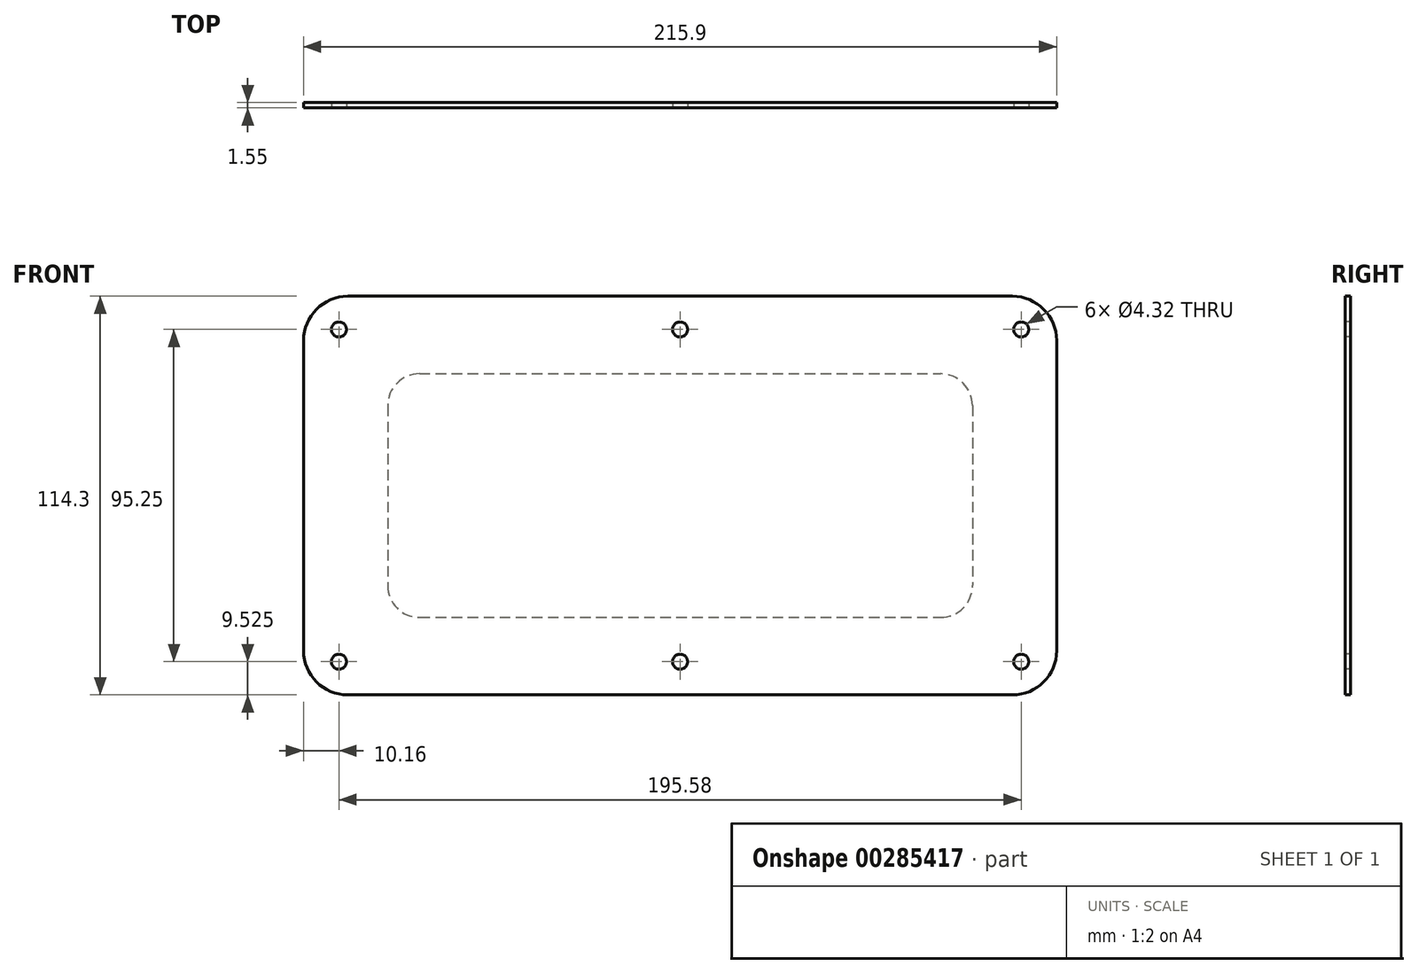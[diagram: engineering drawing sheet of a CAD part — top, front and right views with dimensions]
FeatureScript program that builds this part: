
annotation { "Feature Type Name" : "Feature", "Feature Type Description" : "" }
export const myFeature = defineFeature(function(context is Context, id is Id, definition is map)
    precondition{}
    {
        {
            var Q0;
            Q0=qCreatedBy(makeId("Front.planeOp"),FACE);
            var sketch = newSketch(context, id + "F0", { "sketchPlane" : qUnion([Q0])});
            skLineSegment(sketch, "E0.bottom", {"start": v(33.27, -22.23) * mm, "end": v(182.63, -22.23) * mm, "construction": true});
            skLineSegment(sketch, "E0.top", {"start": v(33.27, -92.08) * mm, "end": v(182.63, -92.08) * mm, "construction": true});
            skLineSegment(sketch, "E0.left", {"start": v(24.13, -31.37) * mm, "end": v(24.13, -82.93) * mm, "construction": true});
            skLineSegment(sketch, "E0.right", {"start": v(191.77, -31.37) * mm, "end": v(191.77, -82.93) * mm, "construction": true});
            skPoint(sketch, "E1.visualSharp", {"position": v(24.13, -22.23) * mm});
            skArc(sketch, "E1.filletArc", {"start": v(33.27, -22.23) * mm, "mid": v(26.8, -24.9) * mm, "end": v(24.13, -31.37) * mm, "construction": true});
            skPoint(sketch, "E2.visualSharp", {"position": v(191.77, -22.23) * mm});
            skArc(sketch, "E2.filletArc", {"start": v(191.77, -31.37) * mm, "mid": v(189.1, -24.9) * mm, "end": v(182.63, -22.22) * mm, "construction": true});
            skPoint(sketch, "E3.visualSharp", {"position": v(191.77, -92.08) * mm});
            skArc(sketch, "E3.filletArc", {"start": v(182.63, -92.08) * mm, "mid": v(189.1, -89.4) * mm, "end": v(191.77, -82.93) * mm, "construction": true});
            skPoint(sketch, "E4.visualSharp", {"position": v(24.13, -92.08) * mm});
            skArc(sketch, "E4.filletArc", {"start": v(24.13, -82.93) * mm, "mid": v(26.8, -89.4) * mm, "end": v(33.27, -92.07) * mm, "construction": true});
            skLineSegment(sketch, "E5.bottom", {"start": v(12.7, 0) * mm, "end": v(203.2, 0) * mm});
            skLineSegment(sketch, "E5.top", {"start": v(12.7, -114.3) * mm, "end": v(203.2, -114.3) * mm});
            skLineSegment(sketch, "E5.left", {"start": v(0, -12.7) * mm, "end": v(0, -101.6) * mm});
            skLineSegment(sketch, "E5.right", {"start": v(215.9, -12.7) * mm, "end": v(215.9, -101.6) * mm});
            skPoint(sketch, "E6.visualSharp", {"position": v(0, 0) * mm});
            skArc(sketch, "E6.filletArc", {"start": v(12.7, 0) * mm, "mid": v(3.72, -3.72) * mm, "end": v(0, -12.7) * mm});
            skPoint(sketch, "E7.visualSharp", {"position": v(215.9, 0) * mm});
            skArc(sketch, "E7.filletArc", {"start": v(215.9, -12.7) * mm, "mid": v(212.18, -3.72) * mm, "end": v(203.2, 0) * mm});
            skPoint(sketch, "E8.visualSharp", {"position": v(215.9, -114.3) * mm});
            skArc(sketch, "E8.filletArc", {"start": v(203.2, -114.3) * mm, "mid": v(212.18, -110.58) * mm, "end": v(215.9, -101.6) * mm});
            skPoint(sketch, "E9.visualSharp", {"position": v(0, -114.3) * mm});
            skArc(sketch, "E9.filletArc", {"start": v(0, -101.6) * mm, "mid": v(3.72, -110.58) * mm, "end": v(12.7, -114.3) * mm});
            skLineSegment(sketch, "E10", {"start": v(107.95, 0) * mm, "end": v(107.95, -114.3) * mm, "construction": true});
            skLineSegment(sketch, "E11", {"start": v(0, -57.15) * mm, "end": v(215.9, -57.15) * mm, "construction": true});
            skPoint(sketch, "E12", {"position": v(107.95, -22.23) * mm});
            skPoint(sketch, "E13", {"position": v(191.77, -57.15) * mm});
            skPoint(sketch, "E14", {"position": v(10.16, -9.52) * mm});
            skPoint(sketch, "E15", {"position": v(107.95, -9.52) * mm});
            skPoint(sketch, "E16", {"position": v(205.74, -9.52) * mm});
            skPoint(sketch, "E17", {"position": v(205.74, -104.78) * mm});
            skPoint(sketch, "E18", {"position": v(107.95, -104.78) * mm});
            skPoint(sketch, "E19", {"position": v(10.16, -104.78) * mm});
            skLineSegment(sketch, "E20", {"start": v(10.16, -9.52) * mm, "end": v(10.16, -104.78) * mm, "construction": true});
            skSolve(sketch);
        }
        {
            var Q0;
            Q0=makeQuery(id+"F0.imprint","IMPRINT",FACE,{"disambiguationData":[TD([[makeQuery(id+"F0.imprint","IMPRINT",EDGE,{"derivedFrom":sQuery(id+"F0.wireOp",EDGE,"E5.bottom")}),-1.0]])]});
            extrude(context, id + "F1", {"entities" : qUnion([Q0]), "depth" : 1.52 * mm});
        }
        {
            var Q0;
            Q0=makeQuery(id+"F1.opExtrude","CAP_FACE",FACE,{"disambiguationData":[OSD([sQuery(id+"F0.wireOp",EDGE,"E5.bottom"),sQuery(id+"F0.wireOp",EDGE,"E5.top"),sQuery(id+"F0.wireOp",EDGE,"E5.left"),sQuery(id+"F0.wireOp",EDGE,"E5.right"),sQuery(id+"F0.wireOp",EDGE,"E6.filletArc"),sQuery(id+"F0.wireOp",EDGE,"E7.filletArc"),sQuery(id+"F0.wireOp",EDGE,"E8.filletArc"),sQuery(id+"F0.wireOp",EDGE,"E9.filletArc")])],"isStart":false});
            var sketch = newSketch(context, id + "F2", { "sketchPlane" : qUnion([Q0])});
            skPoint(sketch, "E21", {"position": v(10.16, -9.52) * mm});
            skPoint(sketch, "E22", {"position": v(107.95, -9.52) * mm});
            skPoint(sketch, "E23", {"position": v(205.74, -9.52) * mm});
            skPoint(sketch, "E24", {"position": v(205.74, -104.78) * mm});
            skPoint(sketch, "E25", {"position": v(107.95, -104.78) * mm});
            skPoint(sketch, "E26", {"position": v(10.16, -104.78) * mm});
            skSolve(sketch);
        }
        {
            var Q0;
            Q0=sQuery(id+"F2.wireOp",VERTEX,"E21");
            var Q1;
            Q1=sQuery(id+"F2.wireOp",VERTEX,"E22");
            var Q2;
            Q2=sQuery(id+"F2.wireOp",VERTEX,"E23");
            var Q3;
            Q3=sQuery(id+"F2.wireOp",VERTEX,"E24");
            var Q4;
            Q4=sQuery(id+"F2.wireOp",VERTEX,"E25");
            var Q5;
            Q5=sQuery(id+"F2.wireOp",VERTEX,"E26");
            var Q6;
            Q6=makeQuery(id+"F1.opExtrude","SWEPT_BODY",BODY,{"disambiguationData":[OSD([sQuery(id+"F0.wireOp",EDGE,"E5.bottom"),sQuery(id+"F0.wireOp",EDGE,"E5.top"),sQuery(id+"F0.wireOp",EDGE,"E5.left"),sQuery(id+"F0.wireOp",EDGE,"E5.right"),sQuery(id+"F0.wireOp",EDGE,"E6.filletArc"),sQuery(id+"F0.wireOp",EDGE,"E7.filletArc"),sQuery(id+"F0.wireOp",EDGE,"E8.filletArc"),sQuery(id+"F0.wireOp",EDGE,"E9.filletArc")])]});
            hole(context, id + "F3", {"style" : HoleStyle.SIMPLE, "endStyle" : HoleEndStyle.THROUGH, "standardTappedOrClearance" : lookupTablePath({ "standard" : "ANSI", "fit" : "Close", "size" : "#8", "type" : "Clearance" }), "standardBlindInLast" : lookupTablePath({ "fit" : "Close", "standard" : "ANSI", "size" : "#8", "type" : "Clearance" }), "holeDiameter" : 4.32 * mm, "isTappedThrough" : true, "tappedDepth" : 2.4 * mm, "tapClearance" : 3, "startFromSketch" : true, "locations" : qUnion([Q0, Q1, Q2, Q3, Q4, Q5]), "scope" : qUnion([Q6]), "majorDiameter" : 6.35 * mm});
        }
        {
            var Q0;
            Q0=makeQuery(id+"F1.opExtrude","CAP_FACE",FACE,{"disambiguationData":[OSD([sQuery(id+"F0.wireOp",EDGE,"E5.bottom"),sQuery(id+"F0.wireOp",EDGE,"E5.top"),sQuery(id+"F0.wireOp",EDGE,"E5.left"),sQuery(id+"F0.wireOp",EDGE,"E5.right"),sQuery(id+"F0.wireOp",EDGE,"E6.filletArc"),sQuery(id+"F0.wireOp",EDGE,"E7.filletArc"),sQuery(id+"F0.wireOp",EDGE,"E8.filletArc"),sQuery(id+"F0.wireOp",EDGE,"E9.filletArc")])],"isStart":true});
            var sketch = newSketch(context, id + "F4", { "sketchPlane" : qUnion([Q0])});
            skLineSegment(sketch, "E27.0", {"start": v(-33.27, -22.23) * mm, "end": v(-182.63, -22.23) * mm});
            skArc(sketch, "E27.1", {"start": v(-33.27, -22.23) * mm, "mid": v(-26.8, -24.9) * mm, "end": v(-24.13, -31.37) * mm});
            skLineSegment(sketch, "E27.2", {"start": v(-24.13, -31.37) * mm, "end": v(-24.13, -82.93) * mm});
            skArc(sketch, "E27.3", {"start": v(-24.13, -82.93) * mm, "mid": v(-26.8, -89.4) * mm, "end": v(-33.27, -92.07) * mm});
            skLineSegment(sketch, "E27.4", {"start": v(-33.27, -92.08) * mm, "end": v(-182.63, -92.08) * mm});
            skArc(sketch, "E27.5", {"start": v(-182.63, -92.08) * mm, "mid": v(-189.1, -89.4) * mm, "end": v(-191.77, -82.93) * mm});
            skLineSegment(sketch, "E27.6", {"start": v(-191.77, -31.37) * mm, "end": v(-191.77, -82.93) * mm});
            skArc(sketch, "E27.7", {"start": v(-191.77, -31.37) * mm, "mid": v(-189.1, -24.9) * mm, "end": v(-182.63, -22.22) * mm});
            skLineSegment(sketch, "E28.0", {"start": v(0, -12.7) * mm, "end": v(0, -101.6) * mm});
            skArc(sketch, "E28.1", {"start": v(-12.7, 0) * mm, "mid": v(-3.72, -3.72) * mm, "end": v(0, -12.7) * mm});
            skLineSegment(sketch, "E28.2", {"start": v(-12.7, 0) * mm, "end": v(-203.2, 0) * mm});
            skArc(sketch, "E28.3", {"start": v(-215.9, -12.7) * mm, "mid": v(-212.18, -3.72) * mm, "end": v(-203.2, 0) * mm});
            skLineSegment(sketch, "E28.4", {"start": v(-215.9, -12.7) * mm, "end": v(-215.9, -101.6) * mm});
            skArc(sketch, "E28.5", {"start": v(-203.2, -114.3) * mm, "mid": v(-212.18, -110.58) * mm, "end": v(-215.9, -101.6) * mm});
            skLineSegment(sketch, "E28.6", {"start": v(-12.7, -114.3) * mm, "end": v(-203.2, -114.3) * mm});
            skArc(sketch, "E28.7", {"start": v(0, -101.6) * mm, "mid": v(-3.72, -110.58) * mm, "end": v(-12.7, -114.3) * mm});
            skCircle(sketch, "E29.0", {"center": v(-205.74, -9.52) * mm, "radius": 2.16 * mm});
            skCircle(sketch, "E30.0", {"center": v(-107.95, -9.52) * mm, "radius": 2.16 * mm});
            skCircle(sketch, "E31.0", {"center": v(-10.16, -9.52) * mm, "radius": 2.16 * mm});
            skCircle(sketch, "E32.0", {"center": v(-10.16, -104.78) * mm, "radius": 2.16 * mm});
            skCircle(sketch, "E33.0", {"center": v(-107.95, -104.78) * mm, "radius": 2.16 * mm});
            skCircle(sketch, "E34.0", {"center": v(-205.74, -104.78) * mm, "radius": 2.16 * mm});
            skSolve(sketch);
        }
        {
            var Q0;
            Q0=qSketchRegion(id+"F4",true);
            extrude(context, id + "F5", {"entities" : qUnion([Q0]), "operationType" : NewBodyOperationType.ADD, "depth" : 0.03 * mm});
        }
    });
